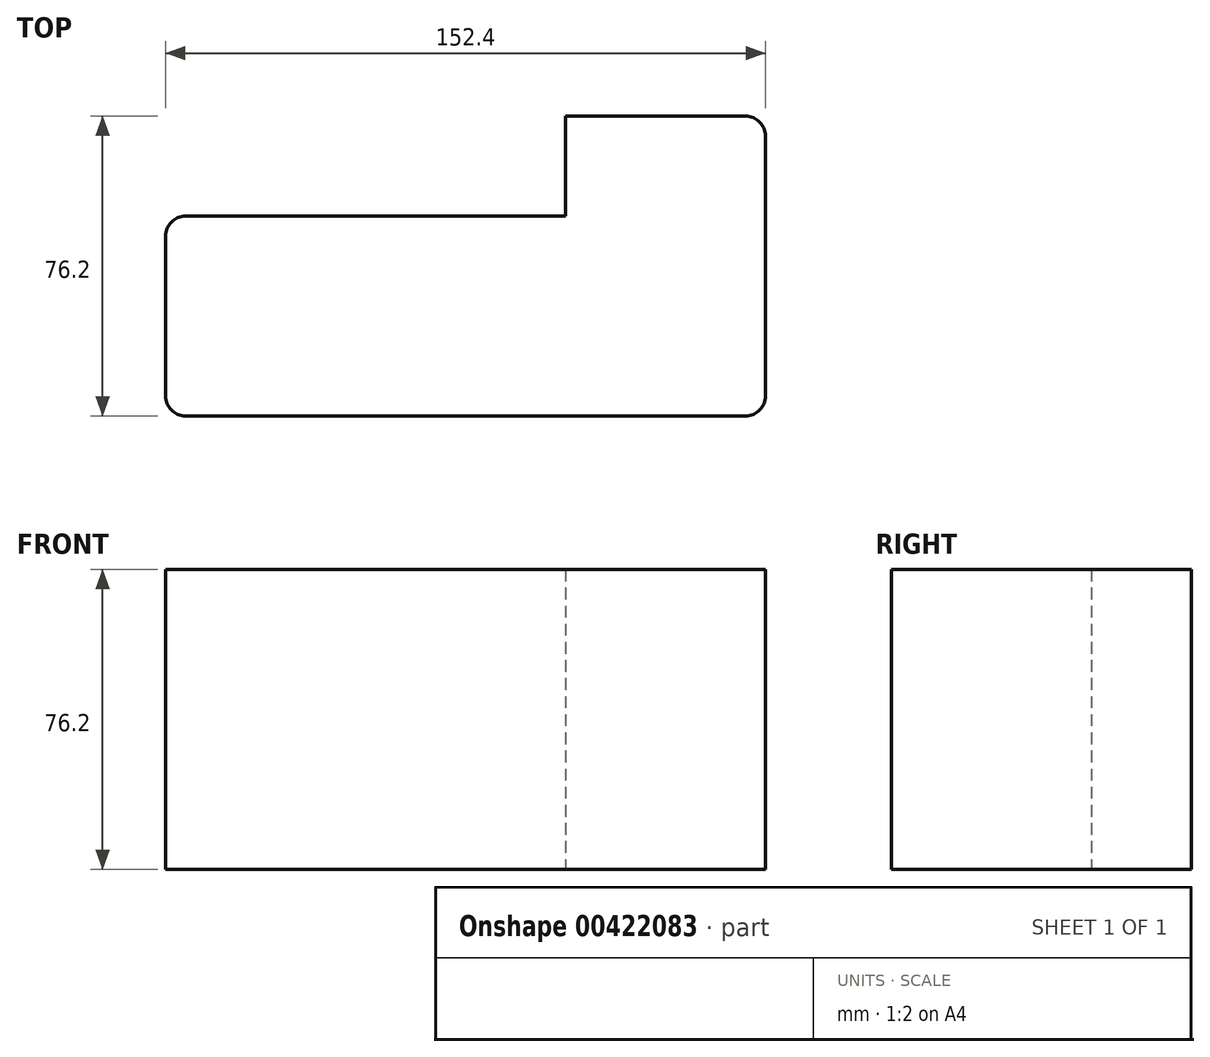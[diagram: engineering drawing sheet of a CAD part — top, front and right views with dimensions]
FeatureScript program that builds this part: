
annotation { "Feature Type Name" : "Feature", "Feature Type Description" : "" }
export const myFeature = defineFeature(function(context is Context, id is Id, definition is map)
    precondition{}
    {
        {
            var Q0;
            Q0=qCreatedBy(makeId("Top.planeOp"),FACE);
            var sketch = newSketch(context, id + "F0", { "sketchPlane" : qUnion([Q0])});
            skLineSegment(sketch, "E0", {"start": v(0, 0) * mm, "end": v(152.4, 0) * mm});
            skLineSegment(sketch, "E1", {"start": v(0, 0) * mm, "end": v(0, 50.8) * mm});
            skLineSegment(sketch, "E2", {"start": v(0, 50.8) * mm, "end": v(101.6, 50.8) * mm});
            skLineSegment(sketch, "E3", {"start": v(101.6, 50.8) * mm, "end": v(101.6, 76.2) * mm});
            skLineSegment(sketch, "E4", {"start": v(101.6, 76.2) * mm, "end": v(152.4, 76.2) * mm});
            skLineSegment(sketch, "E5", {"start": v(152.4, 76.2) * mm, "end": v(152.4, 0) * mm});
            skSolve(sketch);
        }
        {
            var Q0;
            Q0=makeQuery(id+"F0.imprint","IMPRINT",FACE,{"disambiguationData":[TD([[makeQuery(id+"F0.imprint","IMPRINT",EDGE,{"derivedFrom":sQuery(id+"F0.wireOp",EDGE,"E0")}),1.0]])]});
            extrude(context, id + "F1", {"entities" : qUnion([Q0]), "depth" : 50.8 * mm});
        }
        {
            var Q0;
            Q0=makeQuery(id+"F1.opExtrude","SWEPT_EDGE",EDGE,{"disambiguationData":[OSD([sQuery(id+"F0.wireOp",EDGE,"E0"),sQuery(id+"F0.wireOp",EDGE,"E1")])]});
            var Q1;
            Q1=makeQuery(id+"F1.opExtrude","SWEPT_EDGE",EDGE,{"disambiguationData":[OSD([sQuery(id+"F0.wireOp",EDGE,"E1"),sQuery(id+"F0.wireOp",EDGE,"E2")])]});
            var Q2;
            Q2=makeQuery(id+"F1.opExtrude","SWEPT_EDGE",EDGE,{"disambiguationData":[OSD([sQuery(id+"F0.wireOp",EDGE,"E0"),sQuery(id+"F0.wireOp",EDGE,"E5")])]});
            fillet(context, id + "F2", {"entities" : qUnion([Q0, Q1, Q2]), "radius" : 5.08 * mm, "tangentPropagation" : true, "allowEdgeOverflow" : false});
        }
        {
            var Q0;
            Q0=makeQuery(id+"F1.opExtrude","SWEPT_EDGE",EDGE,{"disambiguationData":[OSD([sQuery(id+"F0.wireOp",EDGE,"E4"),sQuery(id+"F0.wireOp",EDGE,"E5")])]});
            fillet(context, id + "F3", {"entities" : qUnion([Q0]), "radius" : 5.08 * mm, "tangentPropagation" : true, "allowEdgeOverflow" : false});
        }
        {
            var Q0;
            Q0 = qSketchRegion(id + "F0", true);
            extrude(context, id + "F4", {"entities" : qUnion([Q0]), "operationType" : NewBodyOperationType.ADD, "depth" : 76.2 * mm});
        }
        {
            var Q0;
            Q0=makeQuery(id+"F4.opExtrude","SWEPT_EDGE",EDGE,{"disambiguationData":[OSD([sQuery(id+"F0.wireOp",EDGE,"E4"),sQuery(id+"F0.wireOp",EDGE,"E5")])]});
            var Q1;
            Q1=makeQuery(id+"F4.opExtrude","SWEPT_EDGE",EDGE,{"disambiguationData":[OSD([sQuery(id+"F0.wireOp",EDGE,"E0"),sQuery(id+"F0.wireOp",EDGE,"E5")])]});
            var Q2;
            Q2=makeQuery(id+"F4.opExtrude","SWEPT_EDGE",EDGE,{"disambiguationData":[OSD([sQuery(id+"F0.wireOp",EDGE,"E0"),sQuery(id+"F0.wireOp",EDGE,"E1")])]});
            var Q3;
            Q3=makeQuery(id+"F4.opExtrude","SWEPT_EDGE",EDGE,{"disambiguationData":[OSD([sQuery(id+"F0.wireOp",EDGE,"E1"),sQuery(id+"F0.wireOp",EDGE,"E2")])]});
            fillet(context, id + "F5", {"entities" : qUnion([Q0, Q1, Q2, Q3]), "radius" : 5.08 * mm, "tangentPropagation" : true, "allowEdgeOverflow" : false});
        }
    });
